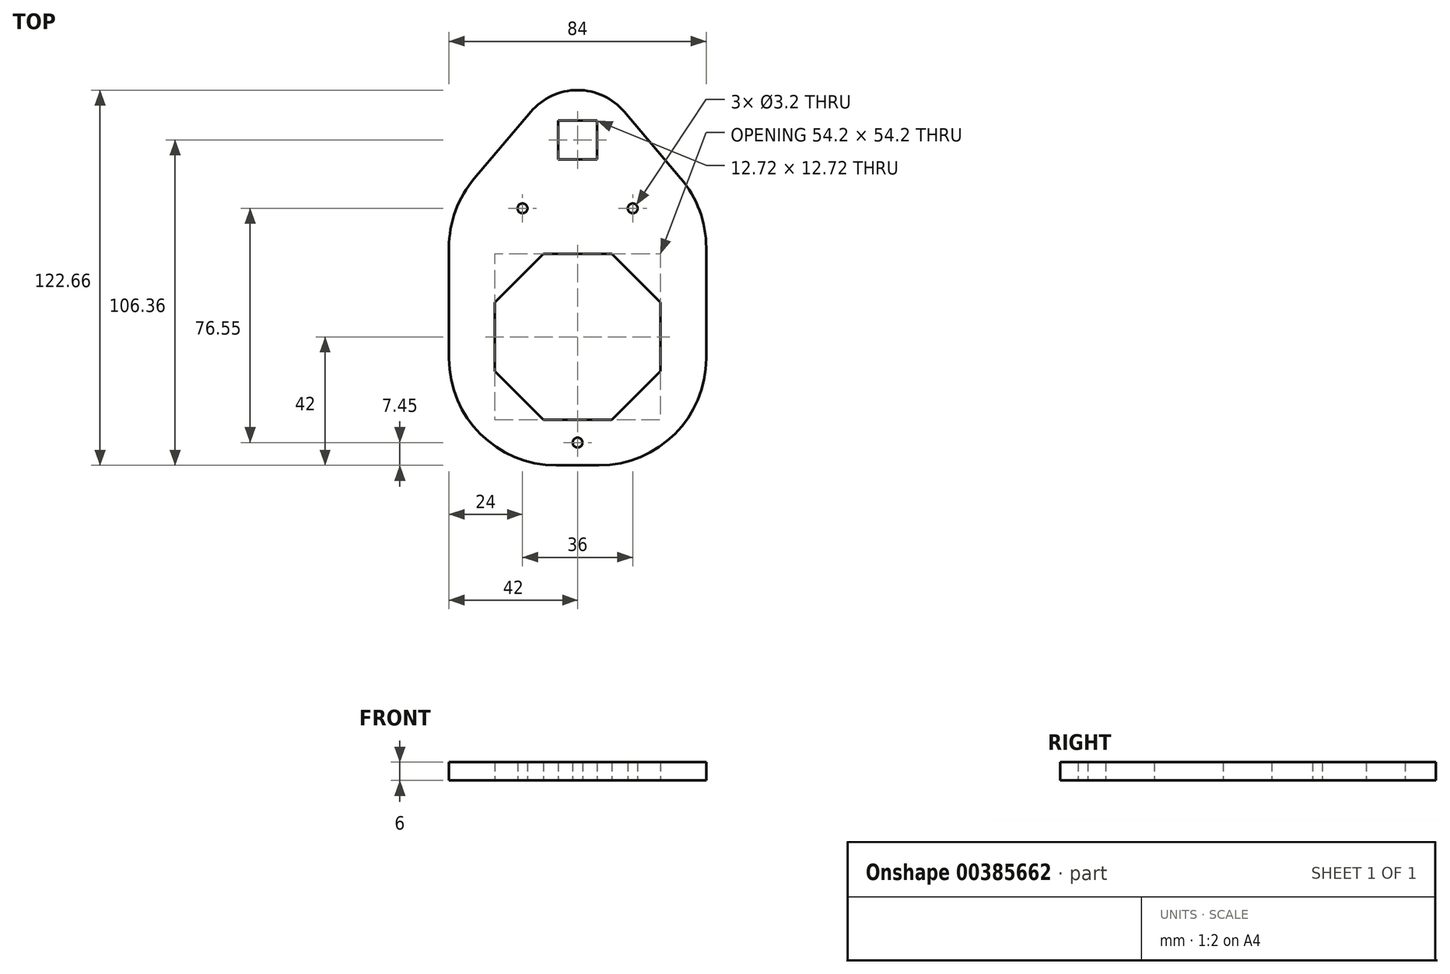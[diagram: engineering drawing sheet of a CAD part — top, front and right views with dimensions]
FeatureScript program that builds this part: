
annotation { "Feature Type Name" : "Feature", "Feature Type Description" : "" }
export const myFeature = defineFeature(function(context is Context, id is Id, definition is map)
    precondition{}
    {
        {
            var Q0;
            Q0=qCreatedBy(makeId("Top.planeOp"),FACE);
            var sketch = newSketch(context, id + "F0", { "sketchPlane" : qUnion([Q0])});
            skLineSegment(sketch, "E0.bottom", {"start": v(0, 0) * mm, "end": v(54.2, 0) * mm, "construction": true});
            skLineSegment(sketch, "E0.top", {"start": v(0, 54.2) * mm, "end": v(54.2, 54.2) * mm, "construction": true});
            skLineSegment(sketch, "E0.left", {"start": v(0, 0) * mm, "end": v(0, 54.2) * mm, "construction": true});
            skLineSegment(sketch, "E0.right", {"start": v(54.2, 0) * mm, "end": v(54.2, 54.2) * mm, "construction": true});
            skLineSegment(sketch, "E1", {"start": v(0, 38.33) * mm, "end": v(15.87, 54.2) * mm});
            skLineSegment(sketch, "E2", {"start": v(38.33, 0) * mm, "end": v(54.2, 15.87) * mm});
            skLineSegment(sketch, "E3", {"start": v(38.33, 54.2) * mm, "end": v(54.2, 38.33) * mm});
            skLineSegment(sketch, "E4", {"start": v(0, 15.87) * mm, "end": v(15.87, 0) * mm});
            skCircle(sketch, "E5", {"center": v(27.1, 27.1) * mm, "radius": 27.1 * mm, "construction": true});
            skPoint(sketch, "E5.centerSnap0", {"position": v(0, 27.1) * mm});
            skPoint(sketch, "E6", {"position": v(27.1, 54.2) * mm});
            skLineSegment(sketch, "E7", {"start": v(-14.9, 69.1) * mm, "end": v(-14.9, -14.9) * mm});
            skLineSegment(sketch, "E8", {"start": v(-14.9, -14.9) * mm, "end": v(69.1, -14.9) * mm});
            skLineSegment(sketch, "E9", {"start": v(69.1, -14.9) * mm, "end": v(69.1, 69.1) * mm});
            skLineSegment(sketch, "E10", {"start": v(69.1, 69.1) * mm, "end": v(-14.9, 69.1) * mm, "construction": true});
            skLineSegment(sketch, "E11", {"start": v(-14.9, 27.1) * mm, "end": v(69.1, 27.1) * mm, "construction": true});
            skLineSegment(sketch, "E12", {"start": v(27.1, -14.9) * mm, "end": v(27.1, 69.1) * mm, "construction": true});
            skLineSegment(sketch, "E13", {"start": v(-14.9, 69.1) * mm, "end": v(27.1, 118.7) * mm});
            skLineSegment(sketch, "E14", {"start": v(69.1, 69.1) * mm, "end": v(27.1, 118.7) * mm});
            skLineSegment(sketch, "E15", {"start": v(0, 38.33) * mm, "end": v(0, 15.87) * mm});
            skLineSegment(sketch, "E16", {"start": v(15.87, 54.2) * mm, "end": v(38.33, 54.2) * mm});
            skLineSegment(sketch, "E17", {"start": v(54.2, 38.33) * mm, "end": v(54.2, 15.87) * mm});
            skLineSegment(sketch, "E18", {"start": v(15.87, 0) * mm, "end": v(38.33, 0) * mm});
            skLineSegment(sketch, "E19.bottom", {"start": v(33.46, 97.82) * mm, "end": v(20.74, 97.82) * mm});
            skLineSegment(sketch, "E19.top", {"start": v(33.46, 85.1) * mm, "end": v(20.74, 85.1) * mm});
            skLineSegment(sketch, "E19.left", {"start": v(33.46, 97.82) * mm, "end": v(33.46, 85.1) * mm});
            skLineSegment(sketch, "E19.right", {"start": v(20.74, 97.82) * mm, "end": v(20.74, 85.1) * mm});
            skLineSegment(sketch, "E20", {"start": v(27.1, 69.1) * mm, "end": v(27.1, 118.7) * mm, "construction": true});
            skPoint(sketch, "E21", {"position": v(27.1, 97.82) * mm});
            skCircle(sketch, "E22", {"center": v(9.1, 69.1) * mm, "radius": 1.6 * mm});
            skCircle(sketch, "E23", {"center": v(45.1, 69.1) * mm, "radius": 1.6 * mm});
            skPoint(sketch, "E24", {"position": v(27.1, 0) * mm});
            skPoint(sketch, "E25", {"position": v(27.1, -7.45) * mm});
            skCircle(sketch, "E26", {"center": v(27.1, -7.45) * mm, "radius": 1.6 * mm});
            skSolve(sketch);
        }
        {
            var Q0;
            Q0=qSketchRegion(id+"F0",true);
            extrude(context, id + "F1", {"entities" : qUnion([Q0]), "depth" : 6 * mm});
        }
        {
            var Q0;
            Q0=makeQuery(id+"F1.opExtrude","SWEPT_EDGE",EDGE,{"disambiguationData":[OSD([sQuery(id+"F0.wireOp",EDGE,"E8"),sQuery(id+"F0.wireOp",EDGE,"E9")])]});
            var Q1;
            Q1=makeQuery(id+"F1.opExtrude","SWEPT_EDGE",EDGE,{"disambiguationData":[OSD([sQuery(id+"F0.wireOp",EDGE,"E7"),sQuery(id+"F0.wireOp",EDGE,"E8")])]});
            var Q2;
            Q2=makeQuery(id+"F1.opExtrude","SWEPT_EDGE",EDGE,{"disambiguationData":[OSD([sQuery(id+"F0.wireOp",EDGE,"E7"),sQuery(id+"F0.wireOp",EDGE,"E10"),sQuery(id+"F0.wireOp",EDGE,"E13")])]});
            var Q3;
            Q3=makeQuery(id+"F1.opExtrude","SWEPT_EDGE",EDGE,{"disambiguationData":[OSD([sQuery(id+"F0.wireOp",EDGE,"E9"),sQuery(id+"F0.wireOp",EDGE,"E10"),sQuery(id+"F0.wireOp",EDGE,"E14")])]});
            fillet(context, id + "F2", {"entities" : qUnion([Q0, Q1, Q2, Q3]), "radius" : 35 * mm, "tangentPropagation" : true, "allowEdgeOverflow" : false});
        }
        {
            var Q0;
            Q0=makeQuery(id+"F1.opExtrude","SWEPT_EDGE",EDGE,{"disambiguationData":[OSD([sQuery(id+"F0.wireOp",EDGE,"E13"),sQuery(id+"F0.wireOp",EDGE,"E14")])]});
            fillet(context, id + "F3", {"entities" : qUnion([Q0]), "radius" : 20 * mm, "tangentPropagation" : true, "allowEdgeOverflow" : false});
        }
    });
